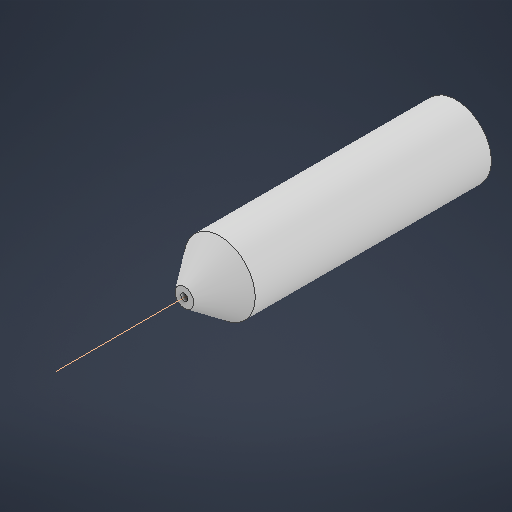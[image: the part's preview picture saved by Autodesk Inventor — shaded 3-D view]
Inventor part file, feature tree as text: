
AUTODESK INVENTOR PART (.ipt)
format: ipt  version: 2025.3 (Build 293356030, 356C)  size: 206,848 bytes
history: native  units: mm
features: sketch x2, extrude x1, revolve x1, other x1
ambient origin geometry x8: Origin, YZ Plane, XZ Plane, XY Plane, X Axis, Y Axis, Z Axis, Center Point
bodies: Solid1 (feature_tree)
feature tree (5):
  extrude  "Extrusion1"  Depth=4.0mm
  revolve  "Revolution1"  [1 undecoded]
  other  "Work Axis1"
  sketch  "Sketch1"  dims[d0=6.0mm d1=4.0mm]
  sketch  "Sketch2"  dims[d2=20.0mm d3=0.0mm d4=3.0mm d6=0.3mm d7=0.5mm d8=90.0deg d5=0.872665mm]
note: 1 required parameter value undecoded (feature->parameter linkage not recoverable at this tier; creation-order binding heuristic only, values carry confidence <= 0.55)
